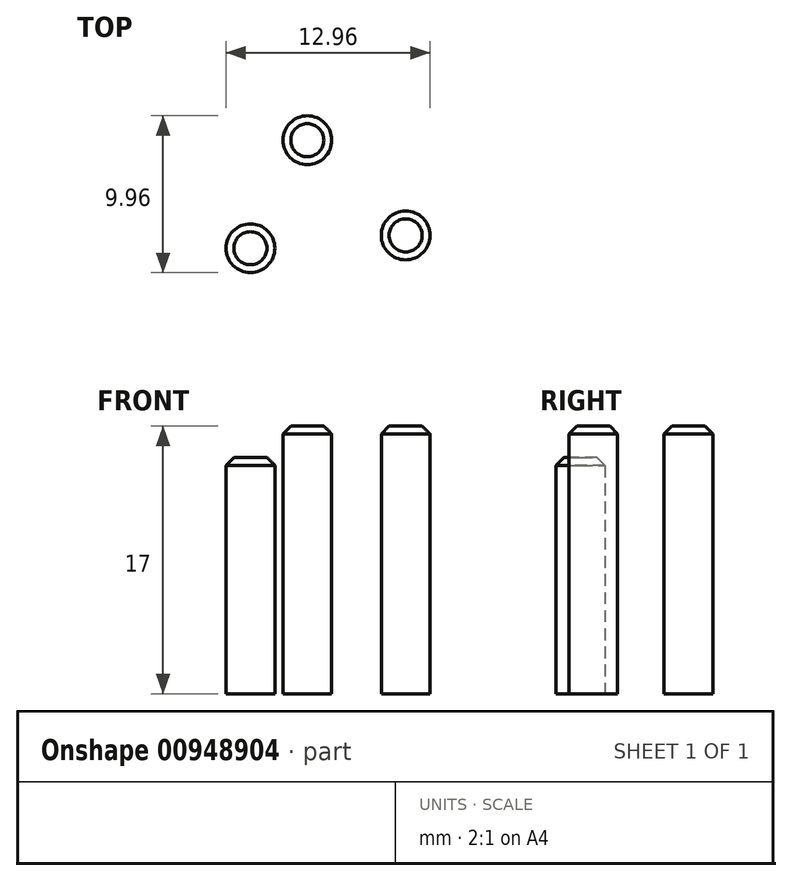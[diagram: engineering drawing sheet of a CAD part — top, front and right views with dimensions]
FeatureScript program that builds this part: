
annotation { "Feature Type Name" : "Feature", "Feature Type Description" : "" }
export const myFeature = defineFeature(function(context is Context, id is Id, definition is map)
    precondition{}
    {
        {
            var Q0;
            Q0=qCreatedBy(makeId("Top.planeOp"),FACE);
            var sketch = newSketch(context, id + "F0", { "sketchPlane" : qUnion([Q0])});
            skCircle(sketch, "E0", {"center": v(0, 0) * mm, "radius": 1.55 * mm});
            skSolve(sketch);
        }
        {
            var Q0;
            Q0=makeQuery(id+"F0.imprint","IMPRINT",FACE,{"disambiguationData":[TD([[makeQuery(id+"F0.imprint","IMPRINT",EDGE,{"derivedFrom":sQuery(id+"F0.wireOp",EDGE,"E0")}),1.0]])]});
            extrude(context, id + "F1", {"entities" : qUnion([Q0]), "depth" : 17 * mm, "offsetDistance" : 25 * mm});
        }
        {
            var Q0;
            Q0=makeQuery(id+"F1.opExtrude","CAP_EDGE",EDGE,{"disambiguationData":[OSD([sQuery(id+"F0.wireOp",EDGE,"E0")])],"isStart":false});
            chamfer(context, id + "F2", {"entities" : qUnion([Q0]), "width" : 0.5 * mm, "tangentPropagation" : true});
        }
        {
            var Q0;
            Q0=qCreatedBy(makeId("Top.planeOp"),FACE);
            var sketch = newSketch(context, id + "F3", { "sketchPlane" : qUnion([Q0])});
            skCircle(sketch, "E1", {"center": v(6.25, -6.05) * mm, "radius": 1.55 * mm});
            skSolve(sketch);
        }
        {
            var Q0;
            Q0=makeQuery(id+"F3.imprint","IMPRINT",FACE,{"disambiguationData":[TD([[makeQuery(id+"F3.imprint","IMPRINT",EDGE,{"derivedFrom":sQuery(id+"F3.wireOp",EDGE,"E1")}),1.0]])]});
            extrude(context, id + "F4", {"entities" : qUnion([Q0]), "depth" : 17 * mm, "offsetDistance" : 25 * mm});
        }
        {
            var Q0;
            Q0=makeQuery(id+"F4.opExtrude","CAP_EDGE",EDGE,{"disambiguationData":[OSD([sQuery(id+"F3.wireOp",EDGE,"E1")])],"isStart":false});
            chamfer(context, id + "F5", {"entities" : qUnion([Q0]), "width" : 0.5 * mm, "tangentPropagation" : true});
        }
        {
            var Q0;
            Q0=qCreatedBy(makeId("Top.planeOp"),FACE);
            var sketch = newSketch(context, id + "F6", { "sketchPlane" : qUnion([Q0])});
            skCircle(sketch, "E2", {"center": v(-3.61, -6.86) * mm, "radius": 1.55 * mm});
            skSolve(sketch);
        }
        {
            var Q0;
            Q0=makeQuery(id+"F6.imprint","IMPRINT",FACE,{"disambiguationData":[TD([[makeQuery(id+"F6.imprint","IMPRINT",EDGE,{"derivedFrom":sQuery(id+"F6.wireOp",EDGE,"E2")}),1.0]])]});
            extrude(context, id + "F7", {"entities" : qUnion([Q0]), "depth" : 15 * mm, "offsetDistance" : 25 * mm});
        }
        {
            var Q0;
            Q0=makeQuery(id+"F7.opExtrude","CAP_EDGE",EDGE,{"disambiguationData":[OSD([sQuery(id+"F6.wireOp",EDGE,"E2")])],"isStart":false});
            chamfer(context, id + "F8", {"entities" : qUnion([Q0]), "width" : 0.5 * mm, "tangentPropagation" : true});
        }
    });
